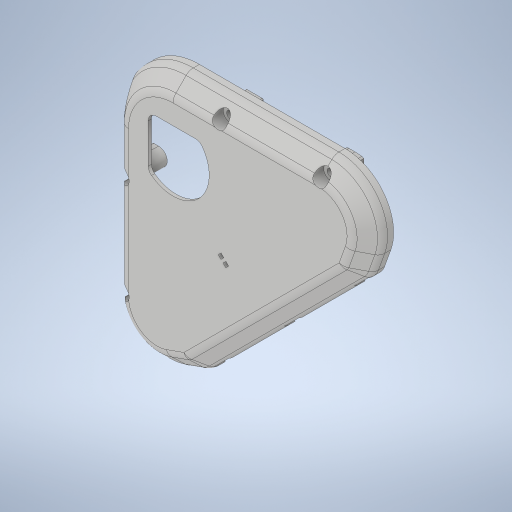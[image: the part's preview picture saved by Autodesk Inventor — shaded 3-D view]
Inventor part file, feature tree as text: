
AUTODESK INVENTOR PART (.ipt)
format: ipt  version: 2023.3 (Build 273359000, 359)  size: 580,096 bytes
history: native  units: in
note: dims shown in document units (in); Inventor stores cm internally (conversion verified against a paired STEP export)
features: sketch x2, extrude x1, hole x1, fillet x1
ambient origin geometry x8: Origin, YZ Plane, XZ Plane, XY Plane, X Axis, Y Axis, Z Axis, Center Point
bodies: Solid2 (feature_tree), Solid1 (feature_tree)
feature tree (5):
  extrude  "Extrusion1"  Depth=0.506in TaperAngle=0.0deg
  hole  "Hole1"  [1 undecoded]
  fillet  "Fillet1"  [1 undecoded]
  sketch  "Sketch1"  dims[d0=0.27in d1=0.506in d2=0.0in]
  sketch  "Sketch2"  dims[d3=0.18in d4=0.75in d5=0.35in d6=0.65in d7=0.563in d8=1.0in d9=0.8108in d10=0.025in]
note: 2 required parameter values undecoded (feature->parameter linkage not recoverable at this tier; creation-order binding heuristic only, values carry confidence <= 0.55)
